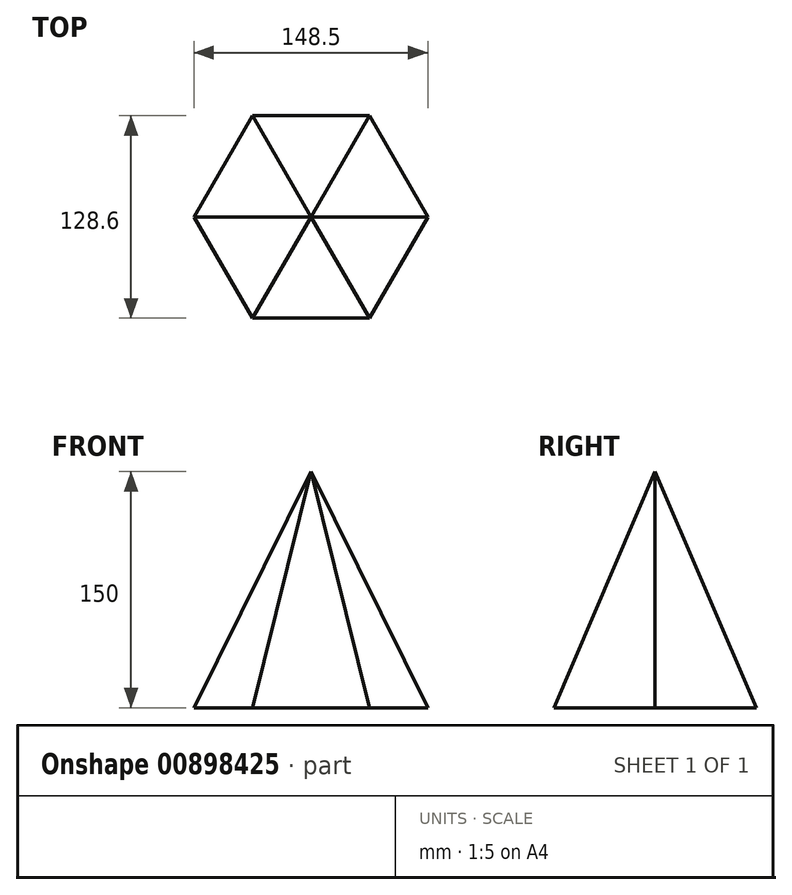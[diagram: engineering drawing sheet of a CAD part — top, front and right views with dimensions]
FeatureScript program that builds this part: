
annotation { "Feature Type Name" : "Feature", "Feature Type Description" : "" }
export const myFeature = defineFeature(function(context is Context, id is Id, definition is map)
    precondition{}
    {
        {
            var Q0;
            Q0=qCreatedBy(makeId("Top.planeOp"),FACE);
            var sketch = newSketch(context, id + "F0", { "sketchPlane" : qUnion([Q0])});
            skCircle(sketch, "E0.cCircle", {"center": v(0, 0) * mm, "radius": 64.3 * mm, "construction": true});
            skLineSegment(sketch, "E0.0", {"start": v(-37.13, 64.3) * mm, "end": v(37.13, 64.3) * mm});
            skLineSegment(sketch, "E0.1", {"start": v(37.13, 64.3) * mm, "end": v(74.25, 0) * mm});
            skLineSegment(sketch, "E0.2", {"start": v(74.25, 0) * mm, "end": v(37.13, -64.3) * mm});
            skLineSegment(sketch, "E0.3", {"start": v(37.13, -64.3) * mm, "end": v(-37.13, -64.3) * mm});
            skLineSegment(sketch, "E0.4", {"start": v(-37.13, -64.3) * mm, "end": v(-74.25, 0) * mm});
            skLineSegment(sketch, "E0.5", {"start": v(-74.25, 0) * mm, "end": v(-37.13, 64.3) * mm});
            skPoint(sketch, "E0.0.midPoint", {"position": v(0, 64.3) * mm});
            skSolve(sketch);
        }
        {
            var Q0;
            Q0=qCreatedBy(makeId("Top.planeOp"),FACE);
            cPlane(context, id + "F1", {"entities" : qUnion([Q0]), "cplaneType" : CPlaneType.OFFSET, "offset" : 150 * mm, "width" : 150 * mm, "height" : 150 * mm});
        }
        {
            var Q0;
            Q0=qCreatedBy(id+"F1.planeOp",FACE);
            var sketch = newSketch(context, id + "F2", { "sketchPlane" : qUnion([Q0])});
            skPoint(sketch, "E1", {"position": v(0, 0) * mm});
            skSolve(sketch);
        }
        {
            var Q0;
            Q0=makeQuery(id+"F0.imprint","IMPRINT",FACE,{"disambiguationData":[TD([[makeQuery(id+"F0.imprint","IMPRINT",EDGE,{"derivedFrom":sQuery(id+"F0.wireOp",EDGE,"E0.0")}),-1.0]])]});
            var Q1;
            Q1=sQuery(id+"F2.wireOp",VERTEX,"E1");
            loft(context, id + "F3", {"sheetProfilesArray" : [{ "sheetProfileEntities" : qUnion([Q0]) }, { "sheetProfileEntities" : qUnion([Q1]) }]});
        }
    });
